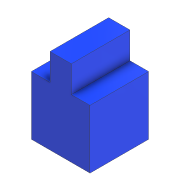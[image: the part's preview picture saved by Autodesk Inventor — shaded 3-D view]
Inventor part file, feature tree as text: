
AUTODESK INVENTOR PART (.ipt)
format: ipt  version: 2021 (Build 250183000, 183)  size: 91,648 bytes
history: native  units: mm
features: extrude x1, sketch x1
ambient origin geometry x8: Origin, YZ Plane, XZ Plane, XY Plane, X Axis, Y Axis, Z Axis, Center Point
bodies: Solid1 (feature_tree)
feature tree (2):
  extrude  "Extrusion1"  Depth=5.5mm
  sketch  "Sketch1"  dims[d0=5.5mm d1=5.5mm d2=2.0mm d3=5.0mm d4=5.5mm d5=0.0mm]
